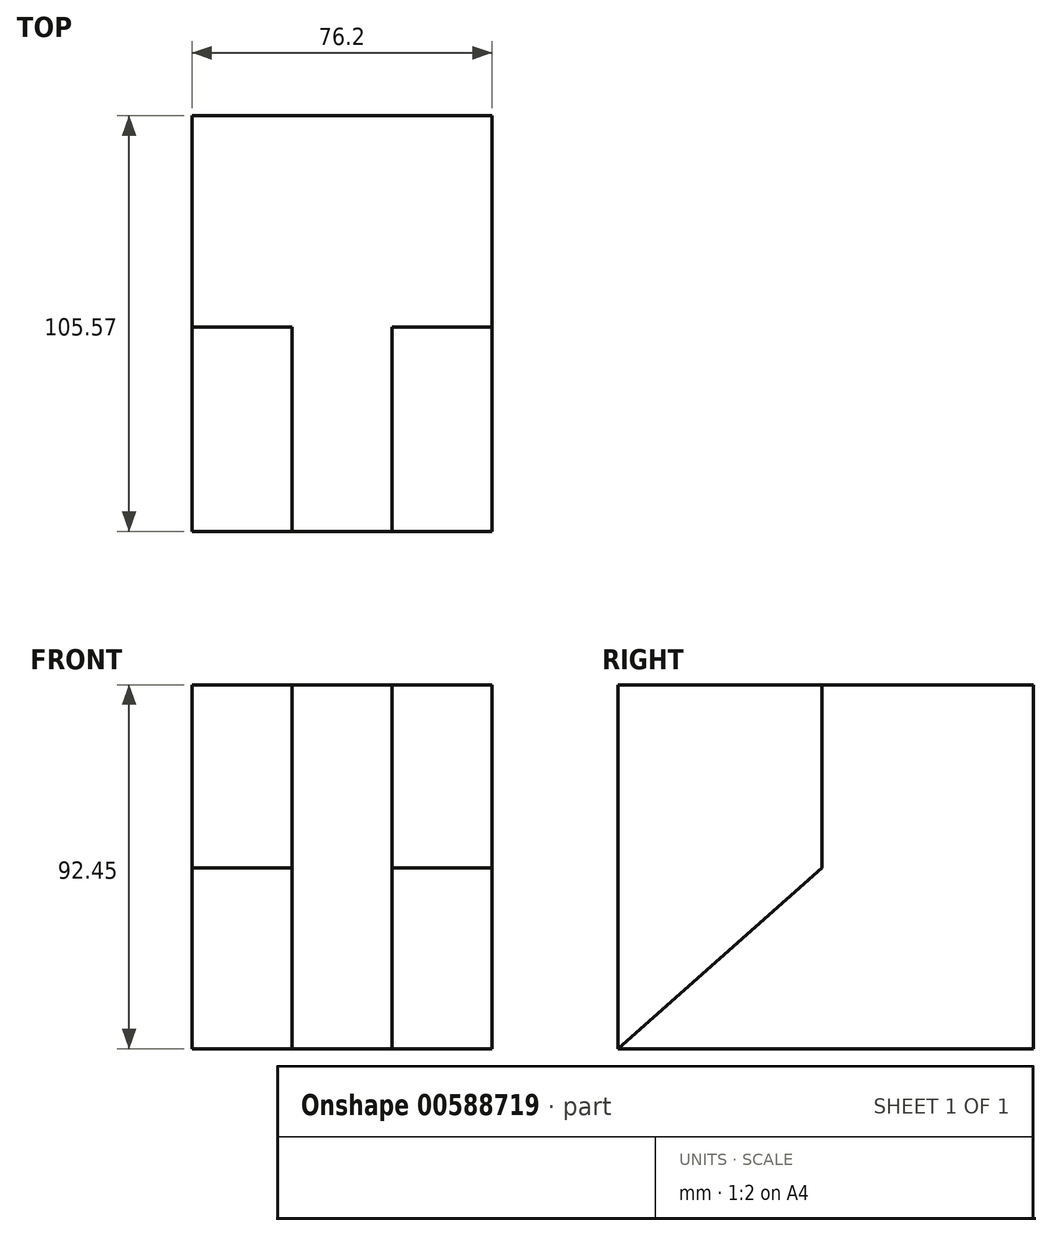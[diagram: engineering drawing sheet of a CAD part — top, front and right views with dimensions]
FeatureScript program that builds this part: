
annotation { "Feature Type Name" : "Feature", "Feature Type Description" : "" }
export const myFeature = defineFeature(function(context is Context, id is Id, definition is map)
    precondition{}
    {
        {
            var Q0;
            Q0=qCreatedBy(makeId("Right.planeOp"),FACE);
            var sketch = newSketch(context, id + "F0", { "sketchPlane" : qUnion([Q0])});
            skLineSegment(sketch, "E0.bottom", {"start": v(-51.9, 46.56) * mm, "end": v(53.67, 46.56) * mm});
            skLineSegment(sketch, "E0.top", {"start": v(-51.9, -45.9) * mm, "end": v(53.67, -45.9) * mm});
            skLineSegment(sketch, "E0.left", {"start": v(-51.9, 46.56) * mm, "end": v(-51.9, -45.9) * mm});
            skLineSegment(sketch, "E0.right", {"start": v(53.67, 46.56) * mm, "end": v(53.67, -45.9) * mm});
            skSolve(sketch);
        }
        {
            var Q0;
            Q0 = qSketchRegion(id + "F0", true);
            extrude(context, id + "F1", {"entities" : qUnion([Q0]), "depth" : 12.7 * mm, "offsetDistance" : 25.4 * mm});
        }
        {
            var Q0;
            Q0=makeQuery(id+"F1.opExtrude","CAP_FACE",FACE,{"disambiguationData":[OSD([sQuery(id+"F0.wireOp",EDGE,"E0.bottom"),sQuery(id+"F0.wireOp",EDGE,"E0.top"),sQuery(id+"F0.wireOp",EDGE,"E0.left"),sQuery(id+"F0.wireOp",EDGE,"E0.right")])],"isStart":true});
            var sketch = newSketch(context, id + "F2", { "sketchPlane" : qUnion([Q0])});
            skSolve(sketch);
        }
        {
            var Q0;
            Q0=makeQuery(id+"F2.imprint","IMPRINT",FACE,{"disambiguationData":[TD([[makeQuery(id+"F2.imprint","IMPRINT",EDGE,{"derivedFrom":makeQuery(id+"F1.opExtrude","CAP_EDGE",EDGE,{"disambiguationData":[OSD([sQuery(id+"F0.wireOp",EDGE,"E0.bottom")])],"isStart":true})}),1.0]])]});
            extrude(context, id + "F3", {"entities" : qUnion([Q0]), "operationType" : NewBodyOperationType.ADD, "depth" : 12.7 * mm, "offsetDistance" : 25.4 * mm});
        }
        {
            var Q0;
            Q0=makeQuery(id+"F3.opExtrude","CAP_FACE",FACE,{"disambiguationData":[OSD([sQuery(id+"F0.wireOp",EDGE,"E0.bottom"),sQuery(id+"F0.wireOp",EDGE,"E0.top"),sQuery(id+"F0.wireOp",EDGE,"E0.left"),sQuery(id+"F0.wireOp",EDGE,"E0.right")])],"isStart":false});
            var sketch = newSketch(context, id + "F4", { "sketchPlane" : qUnion([Q0])});
            skLineSegment(sketch, "E1", {"start": v(0, 0) * mm, "end": v(51.9, -45.9) * mm});
            skLineSegment(sketch, "E2", {"start": v(0, 0) * mm, "end": v(0, 46.56) * mm});
            skSolve(sketch);
        }
        {
            var Q0;
            Q0 = qSketchRegion(id + "F4", true);
            var Q1;
            {var subQ1=sQuery(id+"F4.wireOp",EDGE,"E2");Q1=makeQuery(id+"F4.imprint","IMPRINT",FACE,{"disambiguationData":[TD([[makeQuery(id+"F4.imprint","IMPRINT",EDGE,{"derivedFrom":subQ1}),1.0]])]});}
            extrude(context, id + "F5", {"entities" : qUnion([Q0, Q1]), "operationType" : NewBodyOperationType.ADD, "depth" : 25.4 * mm, "offsetDistance" : 25.4 * mm});
        }
        {
            var Q0;
            Q0=makeQuery(id+"F1.opExtrude","CAP_FACE",FACE,{"disambiguationData":[OSD([sQuery(id+"F0.wireOp",EDGE,"E0.bottom"),sQuery(id+"F0.wireOp",EDGE,"E0.top"),sQuery(id+"F0.wireOp",EDGE,"E0.left"),sQuery(id+"F0.wireOp",EDGE,"E0.right")])],"isStart":false});
            var sketch = newSketch(context, id + "F6", { "sketchPlane" : qUnion([Q0])});
            skLineSegment(sketch, "E3", {"start": v(0, 0) * mm, "end": v(0, 46.56) * mm});
            skLineSegment(sketch, "E4", {"start": v(0, 0) * mm, "end": v(-51.9, -45.9) * mm});
            skSolve(sketch);
        }
        {
            var Q0;
            Q0 = qSketchRegion(id + "F6", true);
            var Q1;
            {var subQ1=sQuery(id+"F6.wireOp",EDGE,"E3");Q1=makeQuery(id+"F6.imprint","IMPRINT",FACE,{"disambiguationData":[TD([[makeQuery(id+"F6.imprint","IMPRINT",EDGE,{"derivedFrom":subQ1}),-1.0]])]});}
            extrude(context, id + "F7", {"entities" : qUnion([Q0, Q1]), "operationType" : NewBodyOperationType.ADD, "depth" : 25.4 * mm, "offsetDistance" : 25.4 * mm});
        }
    });
